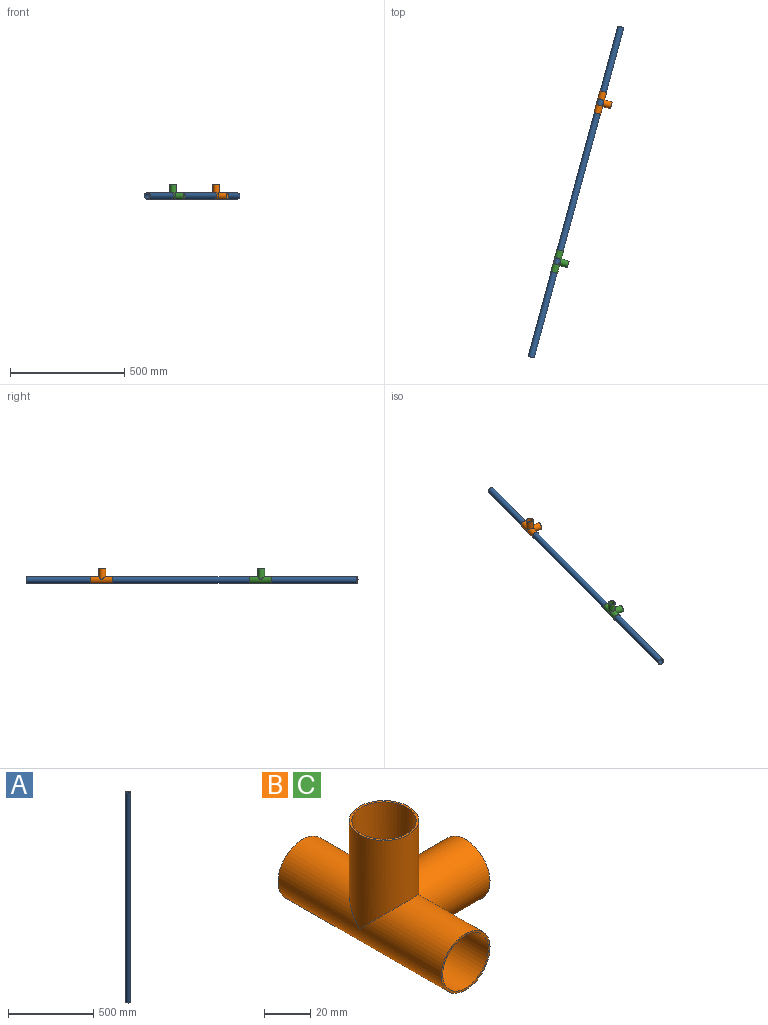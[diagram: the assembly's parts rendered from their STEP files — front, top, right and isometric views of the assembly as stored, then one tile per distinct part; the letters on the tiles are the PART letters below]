
ASSEMBLY  parts=3 mates=2
PART A: 4 faces, bbox 28x28x1500 mm
  f0: cylinder r=13mm len=1500mm, axis (0,0,-1), area 122522.1mm2, adj f2,f3
  f1: cylinder r=14mm len=1500mm, axis (0,0,-1), area 131946.9mm2, adj f2,f3
  f2: plane 28x28mm, normal (0,0,1), area 84.8mm2, adj f0,f1
  f3: plane 28x28mm, normal (0,0,-1), area 84.8mm2, adj f0,f1
PART B: 10 faces, bbox 65x100x65 mm
  f0: cylinder r=14mm len=50mm, axis (0,0,-1), area 3451.9mm2, adj f1,f4,f7
  f1: cylinder r=14mm len=100mm, axis (0,1,0), area 7458.1mm2, adj f0,f5,f6,f7
  f2: cylinder r=15mm len=50mm, axis (0,0,-1), area 3626mm2, adj f3,f4,f8
  f3: cylinder r=15mm len=100mm, axis (0,1,0), area 7888.4mm2, adj f2,f5,f6,f8
  f4: plane 30x30mm, normal (0,0,1), area 91.1mm2, adj f0,f2
  f5: plane 30x30mm, normal (0,-1,0), area 91.1mm2, adj f1,f3
  f6: plane 30x30mm, normal (0,1,0), area 91.1mm2, adj f1,f3
  f7: cylinder r=14mm len=50mm, axis (-1,0,0), area 3451.9mm2, adj f0,f1,f9
  f8: cylinder r=15mm len=50mm, axis (-1,0,0), area 3626mm2, adj f2,f3,f9
  f9: plane 30x30mm, normal (1,0,0), area 91.1mm2, adj f7,f8
PART C: same geometry as B
PLACE A rot(axis=(0.98,-0.13,-0.13),91deg) t=(184.27,687.27,0)mm
PLACE B rot(axis=(0,0,-1),15.2deg) t=(94.36,356.13,0)mm
PLACE C rot(axis=(0,0,-1),15.2deg) t=(-94.74,-340.32,0)mm
MATE slider A.f1 <-> C.f1  axis (0.26,0.97,0) through (-12.26,-36.53,0)mm
MATE slider A.f1 <-> B.f1  axis (0.26,0.97,0) through (-12.26,-36.53,0)mm
